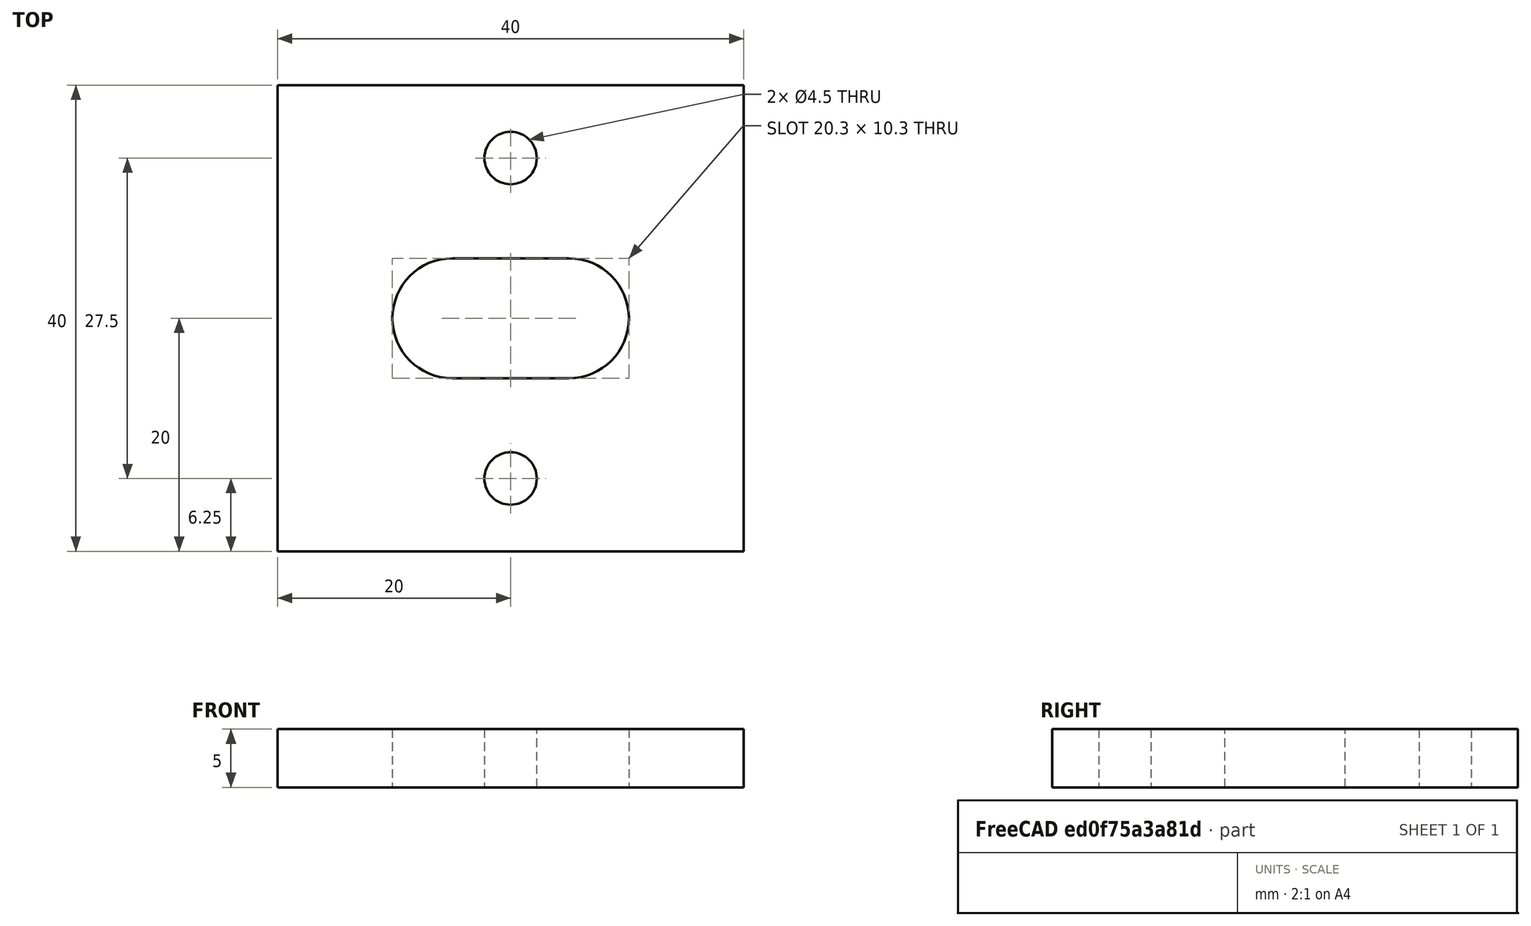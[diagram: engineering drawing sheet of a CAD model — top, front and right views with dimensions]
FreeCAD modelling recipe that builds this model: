
FCSTD DOCUMENT  (FreeCAD 0.15R4477 (Git))
Label: Z-nut-4
License: CC-BY 3.0
LicenseURL: http://creativecommons.org/licenses/by/3.0/
objects: Sketcher::SketchObject×1, PartDesign::Pad×1
note: 3 computed .brp shape members not serialized (recipe doc carries the construction recipe); baked Part::Feature solids carry a one-line shape summary decoded from their .brp

FEATURE [Sketcher::SketchObject] Sketch
  sketch-geometry (10):
    g0: LineSegment StartX=-20 StartY=20 StartZ=0 EndX=20 EndY=20 EndZ=0
    g1: LineSegment StartX=20 StartY=20 StartZ=0 EndX=20 EndY=-20 EndZ=0
    g2: LineSegment StartX=20 StartY=-20 StartZ=0 EndX=-20 EndY=-20 EndZ=0
    g3: LineSegment StartX=-20 StartY=-20 StartZ=0 EndX=-20 EndY=20 EndZ=0
    g4: ArcOfCircle CenterX=-5 CenterY=0 CenterZ=0 NormalX=0 NormalY=0 NormalZ=1 Radius=5.15 StartAngle=1.5708 EndAngle=4.71239
    g5: ArcOfCircle CenterX=5 CenterY=0 CenterZ=0 NormalX=0 NormalY=0 NormalZ=1 Radius=5.15 StartAngle=4.71239 EndAngle=7.85398
    g6: LineSegment StartX=-5 StartY=5.15 StartZ=0 EndX=5 EndY=5.15 EndZ=0
    g7: LineSegment StartX=-5 StartY=-5.15 StartZ=0 EndX=5 EndY=-5.15 EndZ=0
    g8: Circle CenterX=0 CenterY=13.75 CenterZ=0 NormalX=0 NormalY=0 NormalZ=1 Radius=2.25
    g9: Circle CenterX=0 CenterY=-13.75 CenterZ=0 NormalX=0 NormalY=0 NormalZ=1 Radius=2.25
  constraints (32):
    c: Coincident(g0,g1)
    c: Coincident(g1,g2)
    c: Coincident(g2,g3)
    c: Coincident(g3,g0)
    c: Horizontal(g0)
    c: Horizontal(g2)
    c: Vertical(g1)
    c: Vertical(g3)
    c: Symmetric(g2,g1,g-2)
    c: Symmetric(g2,g0,g-1)
    c: Distance(g2) = 40
    c: Distance(g1) = 40
    c: PointOnObject(g4,g-1)
    c: PointOnObject(g5,g-1)
    c: Equal(g4,g5)
    c: Coincident(g6,g4)
    c: Coincident(g6,g5)
    c: Horizontal(g6)
    c: Tangent(g6,g4)
    c: Coincident(g7,g4)
    c: Coincident(g7,g5)
    c: Horizontal(g7)
    c: Tangent(g7,g5)
    c: Radius(g5) = 5.15
    c: Symmetric(g4,g5,g-2)
    c: DistanceX(g4,g5) = 10
    c: PointOnObject(g8,g-2)
    c: Equal(g9,g8)
    c: Radius(g9) = 2.25
    c: PointOnObject(g9,g-2)
    c: DistanceY(g9,g8) = 27.5
    c: Symmetric(g9,g8,g-1)
FEATURE [PartDesign::Pad] Pad
  Length = 5
  Length2 = 100
  Sketch = -> Sketch
  Type = 0
